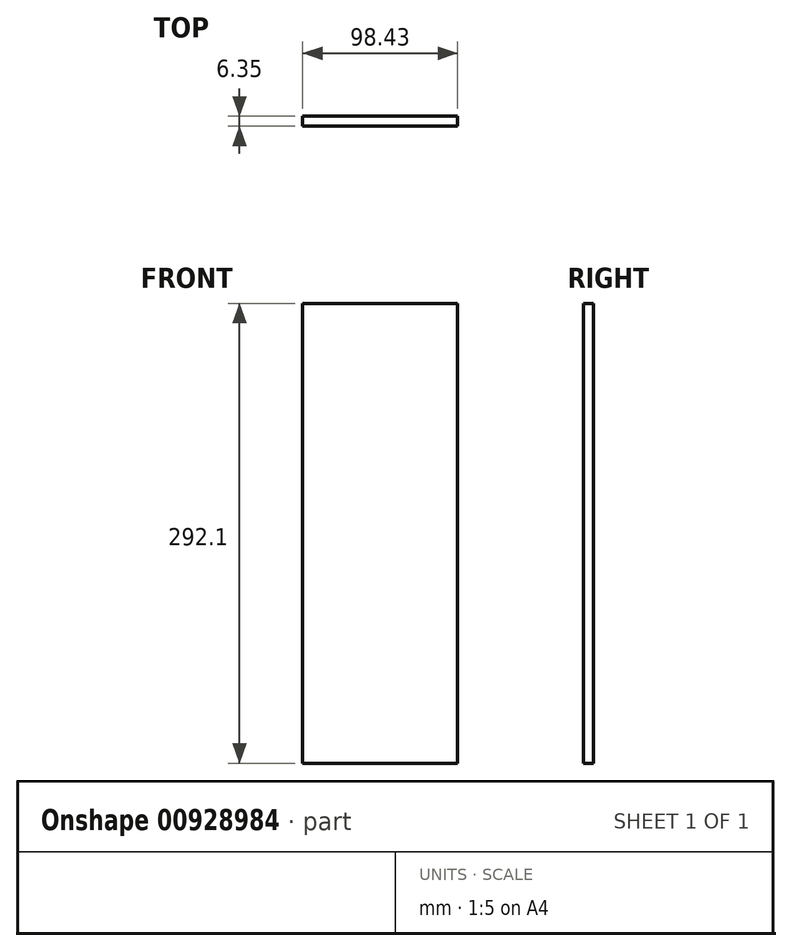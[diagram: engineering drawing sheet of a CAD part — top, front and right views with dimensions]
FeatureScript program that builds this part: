
annotation { "Feature Type Name" : "Feature", "Feature Type Description" : "" }
export const myFeature = defineFeature(function(context is Context, id is Id, definition is map)
    precondition{}
    {
        {
            var Q0;
            Q0=qCreatedBy(makeId("Front.planeOp"),FACE);
            var sketch = newSketch(context, id + "F0", { "sketchPlane" : qUnion([Q0])});
            skLineSegment(sketch, "E0.bottom", {"start": v(-84.08, 172.75) * mm, "end": v(14.35, 172.75) * mm});
            skLineSegment(sketch, "E0.top", {"start": v(-84.08, -119.35) * mm, "end": v(14.35, -119.35) * mm});
            skLineSegment(sketch, "E0.left", {"start": v(-84.08, 172.75) * mm, "end": v(-84.08, -119.35) * mm});
            skLineSegment(sketch, "E0.right", {"start": v(14.35, 172.75) * mm, "end": v(14.35, -119.35) * mm});
            skSolve(sketch);
        }
        {
            var Q0;
            Q0=qSketchRegion(id+"F0",true);
            extrude(context, id + "F1", {"entities" : qUnion([Q0]), "flatOperationType" : FlatOperationType.REMOVE, "thickness" : 6.35 * mm, "thickness2" : 0 * mm, "thickness1" : 6.35 * mm, "depth" : 6.35 * mm, "offsetDistance" : 25.4 * mm, "startOffsetDistance" : 25.4 * mm, "startOffsetBound" : StartOffsetType.BLIND, "domain" : OperationDomain.MODEL});
        }
    });
